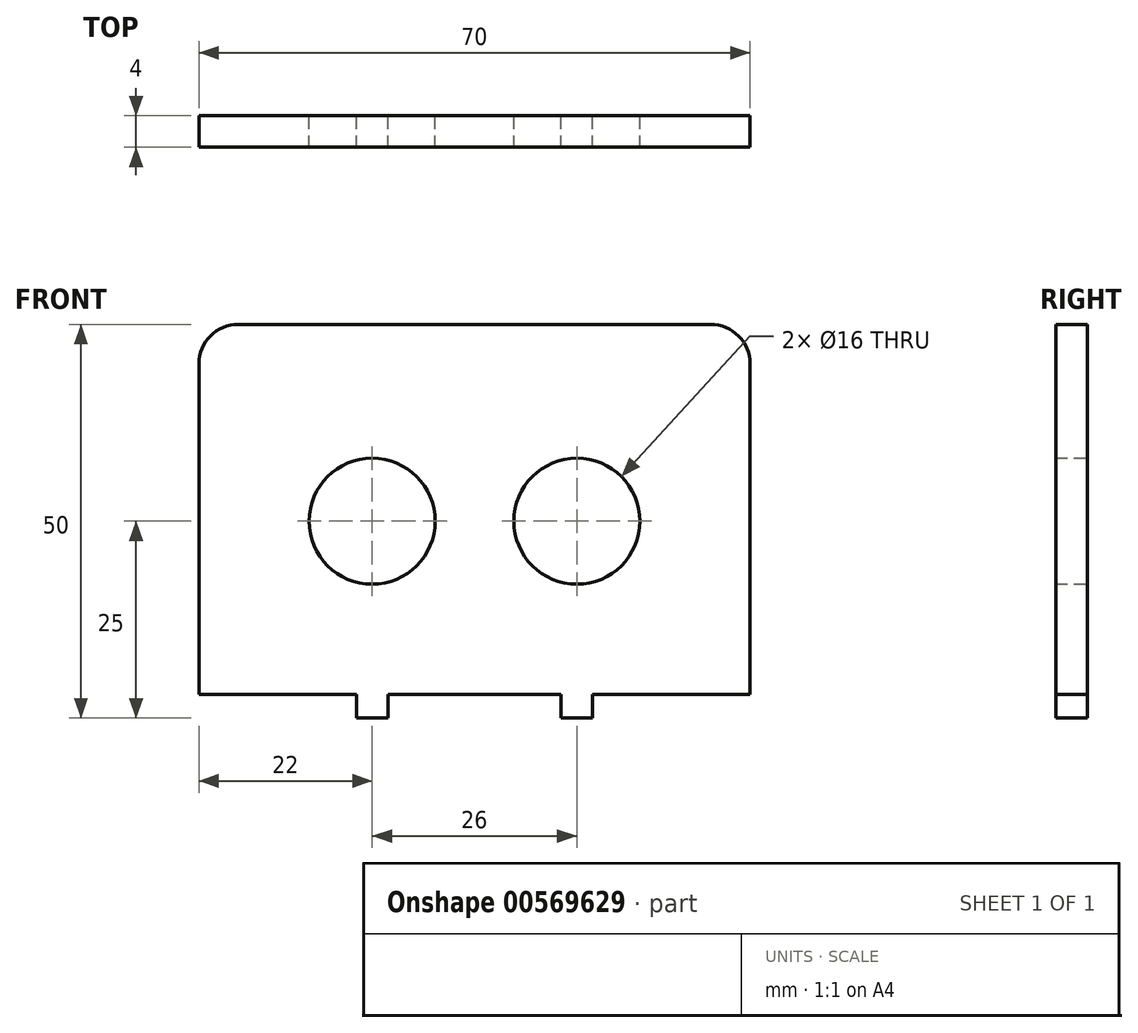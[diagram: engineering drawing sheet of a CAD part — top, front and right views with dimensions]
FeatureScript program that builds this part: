
annotation { "Feature Type Name" : "Feature", "Feature Type Description" : "" }
export const myFeature = defineFeature(function(context is Context, id is Id, definition is map)
    precondition{}
    {
        {
            var Q0;
            Q0=qCreatedBy(makeId("Front.planeOp"),FACE);
            var sketch = newSketch(context, id + "F0", { "sketchPlane" : qUnion([Q0])});
            skLineSegment(sketch, "E0.bottom", {"start": v(-30, 25) * mm, "end": v(30, 25) * mm});
            skLineSegment(sketch, "E0.top", {"start": v(-15, -25) * mm, "end": v(-11, -25) * mm});
            skLineSegment(sketch, "E0.left", {"start": v(-35, 20) * mm, "end": v(-35, -22) * mm});
            skLineSegment(sketch, "E0.right", {"start": v(35, 20) * mm, "end": v(35, -22) * mm});
            skCircle(sketch, "E1", {"center": v(-13, 0) * mm, "radius": 8 * mm});
            skCircle(sketch, "E2", {"center": v(13, 0) * mm, "radius": 8 * mm});
            skLineSegment(sketch, "E3", {"start": v(0, 0) * mm, "end": v(-21, 0) * mm, "construction": true});
            skLineSegment(sketch, "E4", {"start": v(0, 0) * mm, "end": v(35, 0) * mm, "construction": true});
            skLineSegment(sketch, "E5", {"start": v(-13, 3.27) * mm, "end": v(-13, 0) * mm});
            skPoint(sketch, "E6.visualSharp", {"position": v(-35, 25) * mm});
            skArc(sketch, "E6.filletArc", {"start": v(-30, 25) * mm, "mid": v(-33.54, 23.54) * mm, "end": v(-35, 20) * mm});
            skPoint(sketch, "E7.visualSharp", {"position": v(35, 25) * mm});
            skArc(sketch, "E7.filletArc", {"start": v(35, 20) * mm, "mid": v(33.54, 23.54) * mm, "end": v(30, 25) * mm});
            skLineSegment(sketch, "E8", {"start": v(-40.83, -22) * mm, "end": v(42.02, -22) * mm, "construction": true});
            skLineSegment(sketch, "E9", {"start": v(-35, -22) * mm, "end": v(-15, -22) * mm});
            skLineSegment(sketch, "E10", {"start": v(-15, -22) * mm, "end": v(-15, -25) * mm});
            skLineSegment(sketch, "E11", {"start": v(-11, -25) * mm, "end": v(-11, -22) * mm});
            skLineSegment(sketch, "E12", {"start": v(-11, -22) * mm, "end": v(11, -22) * mm});
            skLineSegment(sketch, "E13", {"start": v(11, -22) * mm, "end": v(11, -25) * mm});
            skLineSegment(sketch, "E14", {"start": v(11, -25) * mm, "end": v(15, -25) * mm});
            skLineSegment(sketch, "E15", {"start": v(15, -25) * mm, "end": v(15, -22) * mm});
            skLineSegment(sketch, "E16", {"start": v(15, -22) * mm, "end": v(35, -22) * mm});
            skPoint(sketch, "E17.orphan", {"position": v(-35, -25) * mm});
            skPoint(sketch, "E18.orphan", {"position": v(35, -25) * mm});
            skSolve(sketch);
        }
        {
            var Q0;
            Q0=makeQuery(id+"F0.imprint","IMPRINT",FACE,{"disambiguationData":[TD([[makeQuery(id+"F0.imprint","IMPRINT",EDGE,{"derivedFrom":sQuery(id+"F0.wireOp",EDGE,"E0.bottom")}),-1.0]])]});
            extrude(context, id + "F1", {"entities" : qUnion([Q0]), "depth" : 4 * mm, "offsetDistance" : 25 * mm});
        }
    });
